# Revit family: Door-Automatic_Fire_Vent-Bilco-Single_Leaf
name_source: partatom
category: Doors
units: mm (PartAtom-declared; Revit-internal decimal feet)

## family parameters
Cut with Voids When Loaded = No
Host = Face
OmniClass Number = 23.30.10.27.24
OmniClass Title = Roof Hatches
Room Calculation Point = No
Shared = No

## types (2) — shared parameters
Analytic Construction = <None>
Cover Length = 34"
Cover Material = Galvanized Steel-Bilco-Red Oxide Primer Finish
Cover Opening = 90.00°
Cover Width = 41 1/4"
Default Elevation = 48"
Description = Automatic Fire Vent
Dome Material = Plastic-Bilco-Polycarbonate
Frame Exterior Length = 34"
Frame Exterior Width = 40"
Frame Type = Frame-Bilco-1in_Fiberboard_Insulation
Gasket Material = Plastic-Bilco-Rubber Black
Hardware Material = Stainless Steel-Bilco-Sand Blast Finish-304
Height = 12 19/32"
Length = 30"
Manufacturer = Bilco
Model = GS-SV
Product Documentation Link = http://www.bilco.com
Product Page URL = https://www.bilco.com
Rough Height = 30"
Rough Width = 36"
URL = http://www.bilco.com
Width = 36"

## per-type parameters (varying)
| type | Cover Type | Fiberboard Insulation Material | Frame Material |
| SV | Cover-Bilco-1in_Fiberglass_Insulation | Stainless Steel-Bilco-Sand Blast Finish-304 | Galvanized Steel-Bilco-Red Oxide Primer Finish |
| GS-SV | Cover-Bilco-Polycarbonate_Dome | Insulation-Bilco-Rigid Insulation | Stainless Steel-Bilco-Sand Blast Finish-304 |

## geometry (parser evidence)
native form markers: Sweep x27
no freeform markers — native parametric forms only
